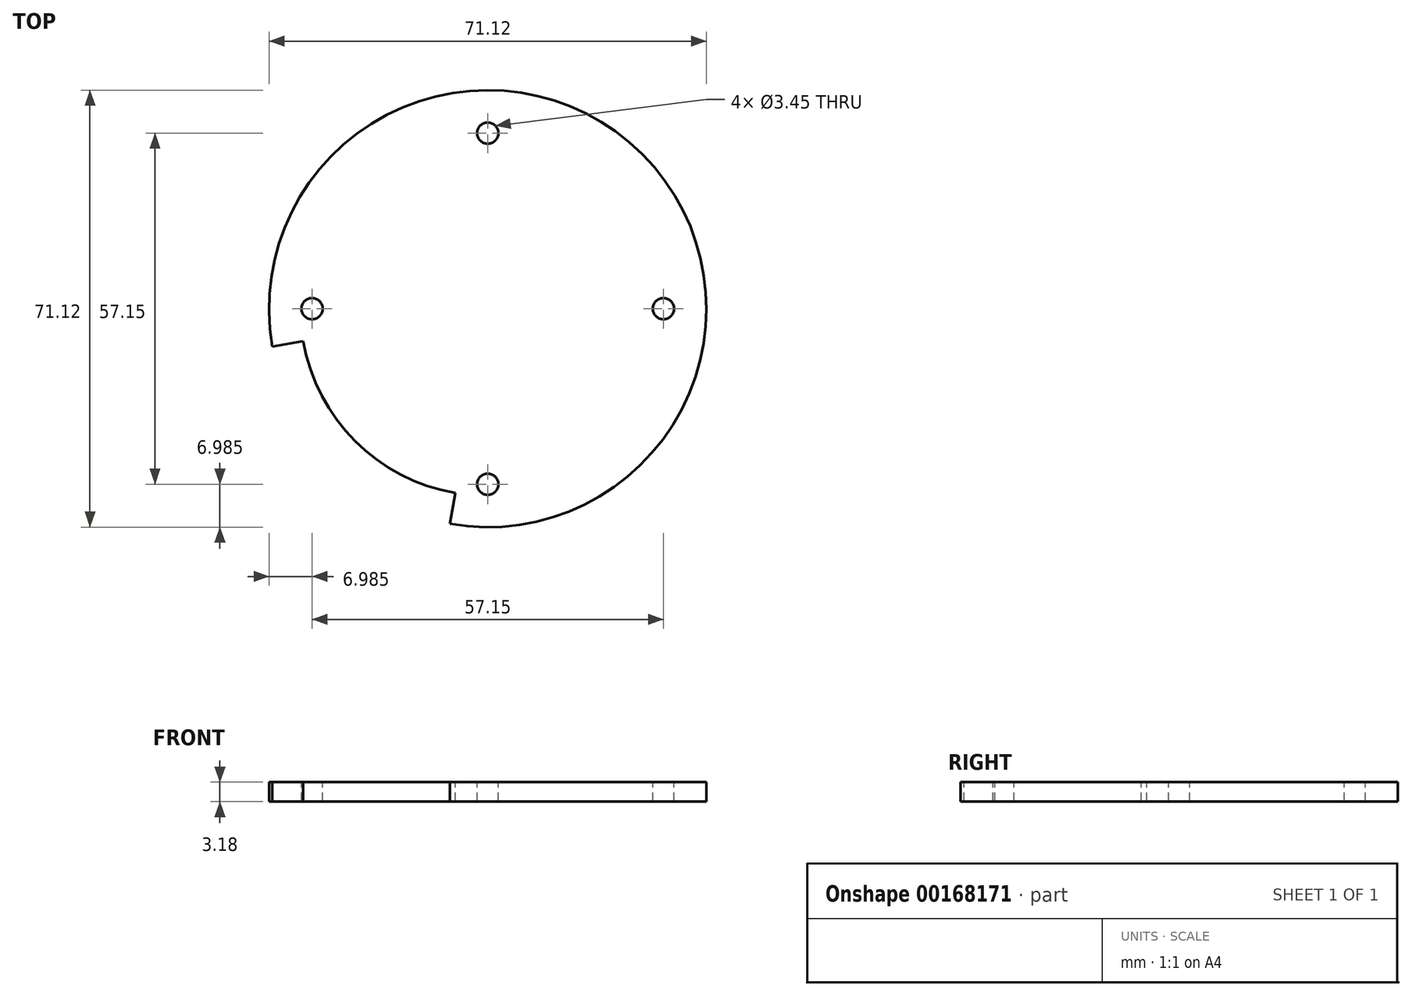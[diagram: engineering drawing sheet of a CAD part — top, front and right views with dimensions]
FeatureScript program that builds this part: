
annotation { "Feature Type Name" : "Feature", "Feature Type Description" : "" }
export const myFeature = defineFeature(function(context is Context, id is Id, definition is map)
    precondition{}
    {
        {
            var Q0;
            Q0=qCreatedBy(makeId("Top.planeOp"),FACE);
            var sketch = newSketch(context, id + "F0", { "sketchPlane" : qUnion([Q0])});
            skCircle(sketch, "E0", {"center": v(0, 0) * mm, "radius": 35.56 * mm});
            skSolve(sketch);
        }
        {
            var Q0;
            Q0=makeQuery(id+"F0.imprint","IMPRINT",FACE,{"disambiguationData":[TD([[makeQuery(id+"F0.imprint","IMPRINT",EDGE,{"derivedFrom":sQuery(id+"F0.wireOp",EDGE,"E0")}),1.0]])]});
            extrude(context, id + "F1", {"entities" : qUnion([Q0]), "depth" : 3.17 * mm});
        }
        {
            var Q0;
            {var subQ0=makeQuery(id+"FhJubWmbG7UBd7M_1.boolean.opBoolean","COPY",FACE,{"derivedFrom":makeQuery(id+"FhJubWmbG7UBd7M_1.opExtrude","SWEPT_FACE",FACE,{"disambiguationData":[OSD([sQuery(id+"FRuIeaWD6VeLny9_1.wireOp",EDGE,"idePJaX5-tPPE-BKw2-N1m4-zZUQrY6AHjir")])]})});Q0=makeQuery(id+"FOQC5dfjhO448EJ_1.boolean.opBoolean","SPLIT",FACE,{"disambiguationData":[TD([subQ0])],"derivedFrom":makeQuery(id+"FkcieFRIapZdHPD_1.boolean.opBoolean","SPLIT",FACE,{"disambiguationData":[TD([subQ0])],"derivedFrom":makeQuery(id+"F1.opExtrude","CAP_FACE",FACE,{"disambiguationData":[OSD([sQuery(id+"F0.wireOp",EDGE,"E0")])],"isStart":false})})});}
            var sketch = newSketch(context, id + "F2", { "sketchPlane" : qUnion([Q0])});
            skCircle(sketch, "E1", {"center": v(0, 0) * mm, "radius": 28.58 * mm, "construction": true});
            skLineSegment(sketch, "E2", {"start": v(0, 0) * mm, "end": v(28.58, 0) * mm, "construction": true});
            skPoint(sketch, "E3", {"position": v(28.58, 0) * mm});
            skLineSegment(sketch, "E4", {"start": v(0, 0) * mm, "end": v(-28.58, 0) * mm, "construction": true});
            skPoint(sketch, "E5", {"position": v(-28.58, 0) * mm});
            skPoint(sketch, "E6.1.0", {"position": v(0, -28.58) * mm});
            skPoint(sketch, "E6.3.0", {"position": v(0, 28.58) * mm});
            skSolve(sketch);
        }
        {
            var Q0;
            Q0=sQuery(id+"F2.wireOp",VERTEX,"E5");
            var Q1;
            Q1=sQuery(id+"F2.wireOp",VERTEX,"E6.3.0");
            var Q2;
            Q2=sQuery(id+"F2.wireOp",VERTEX,"E3");
            var Q3;
            Q3=sQuery(id+"F2.wireOp",VERTEX,"E6.1.0");
            var Q4;
            Q4=makeQuery(id+"F1.opExtrude","SWEPT_BODY",BODY,{"disambiguationData":[OSD([sQuery(id+"F0.wireOp",EDGE,"E0")])]});
            hole(context, id + "F3", {"style" : HoleStyle.SIMPLE, "endStyle" : HoleEndStyle.BLIND, "standardTappedOrClearance" : lookupTablePath({ "standard" : "ANSI", "engagement" : "75%", "pitch" : "32 tpi", "size" : "#8", "type" : "Tapped" }), "standardBlindInLast" : lookupTablePath({ "standard" : "ANSI", "engagement" : "75%", "pitch" : "32 tpi", "size" : "#8", "type" : "Tapped" }), "holeDiameter" : 3.45 * mm, "holeDepth" : 11.43 * mm, "locations" : qUnion([Q0, Q1, Q2, Q3]), "scope" : qUnion([Q4]), "majorDiameter" : 4.17 * mm});
        }
        {
            var Q0;
            Q0=makeQuery(id+"F1.opExtrude","CAP_FACE",FACE,{"disambiguationData":[OSD([sQuery(id+"F0.wireOp",EDGE,"E0")])],"isStart":false});
            var sketch = newSketch(context, id + "F4", { "sketchPlane" : qUnion([Q0])});
            skArc(sketch, "E7", {"start": v(-30.02, -5.3) * mm, "mid": v(-21.55, -21.55) * mm, "end": v(-5.3, -30.02) * mm});
            skLineSegment(sketch, "E8", {"start": v(-5.3, -30.02) * mm, "end": v(0, 0) * mm, "construction": true});
            skLineSegment(sketch, "E9", {"start": v(0, 0) * mm, "end": v(-30.02, -5.3) * mm, "construction": true});
            skLineSegment(sketch, "E10", {"start": v(-30.02, -5.3) * mm, "end": v(-35.02, -6.17) * mm});
            skLineSegment(sketch, "E11", {"start": v(-6.17, -35.02) * mm, "end": v(-5.3, -30.02) * mm});
            skArc(sketch, "E12", {"start": v(-6.17, -35.02) * mm, "mid": v(-25.14, -25.14) * mm, "end": v(-35.02, -6.17) * mm});
            skSolve(sketch);
        }
        {
            var Q0;
            Q0 = qSketchRegion(id + "F4", true);
            extrude(context, id + "F5", {"entities" : qUnion([Q0]), "operationType" : NewBodyOperationType.REMOVE, "endBound" : BoundingType.THROUGH_ALL, "oppositeDirection" : true, "depth" : 25.4 * mm});
        }
    });
